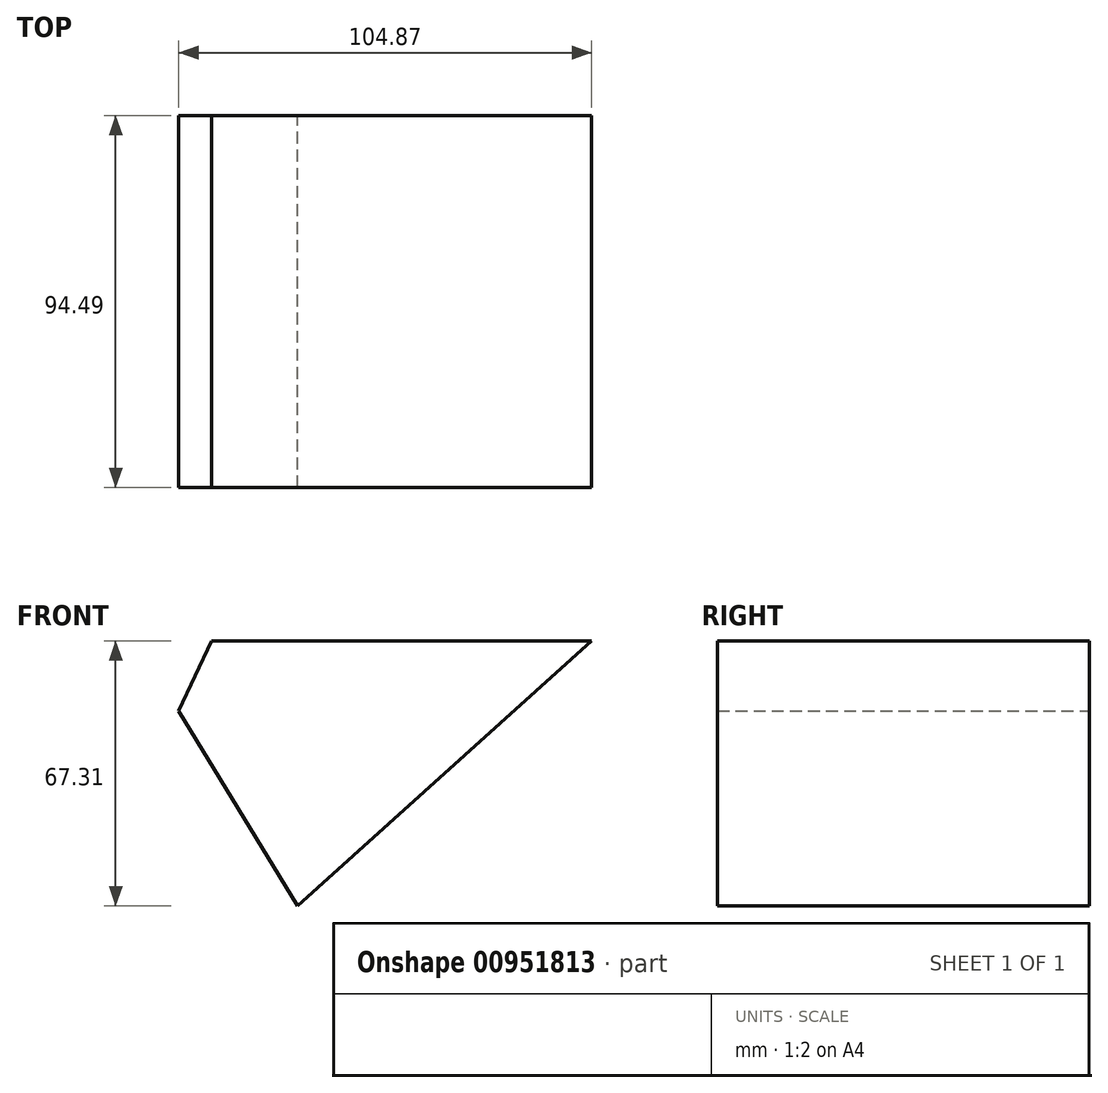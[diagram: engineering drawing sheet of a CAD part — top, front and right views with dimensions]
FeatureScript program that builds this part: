
annotation { "Feature Type Name" : "Feature", "Feature Type Description" : "" }
export const myFeature = defineFeature(function(context is Context, id is Id, definition is map)
    precondition{}
    {
        {
            var Q0;
            Q0=qCreatedBy(makeId("Front.planeOp"),FACE);
            var sketch = newSketch(context, id + "F0", { "sketchPlane" : qUnion([Q0])});
            skLineSegment(sketch, "E0", {"start": v(-129.64, 75.41) * mm, "end": v(-33.17, 75.41) * mm});
            skLineSegment(sketch, "E1", {"start": v(-33.17, 75.41) * mm, "end": v(-107.91, 8.1) * mm});
            skLineSegment(sketch, "E2", {"start": v(-107.91, 8.1) * mm, "end": v(-138.04, 57.63) * mm});
            skLineSegment(sketch, "E3", {"start": v(-138.04, 57.63) * mm, "end": v(-129.64, 75.41) * mm});
            skSolve(sketch);
        }
        {
            var Q0;
            Q0=makeQuery(id+"F0.imprint","IMPRINT",FACE,{"disambiguationData":[TD([[makeQuery(id+"F0.imprint","IMPRINT",EDGE,{"derivedFrom":sQuery(id+"F0.wireOp",EDGE,"E0")}),-1.0]])]});
            extrude(context, id + "F1", {"entities" : qUnion([Q0]), "depth" : 94.49 * mm, "offsetDistance" : 25.4 * mm});
        }
    });
